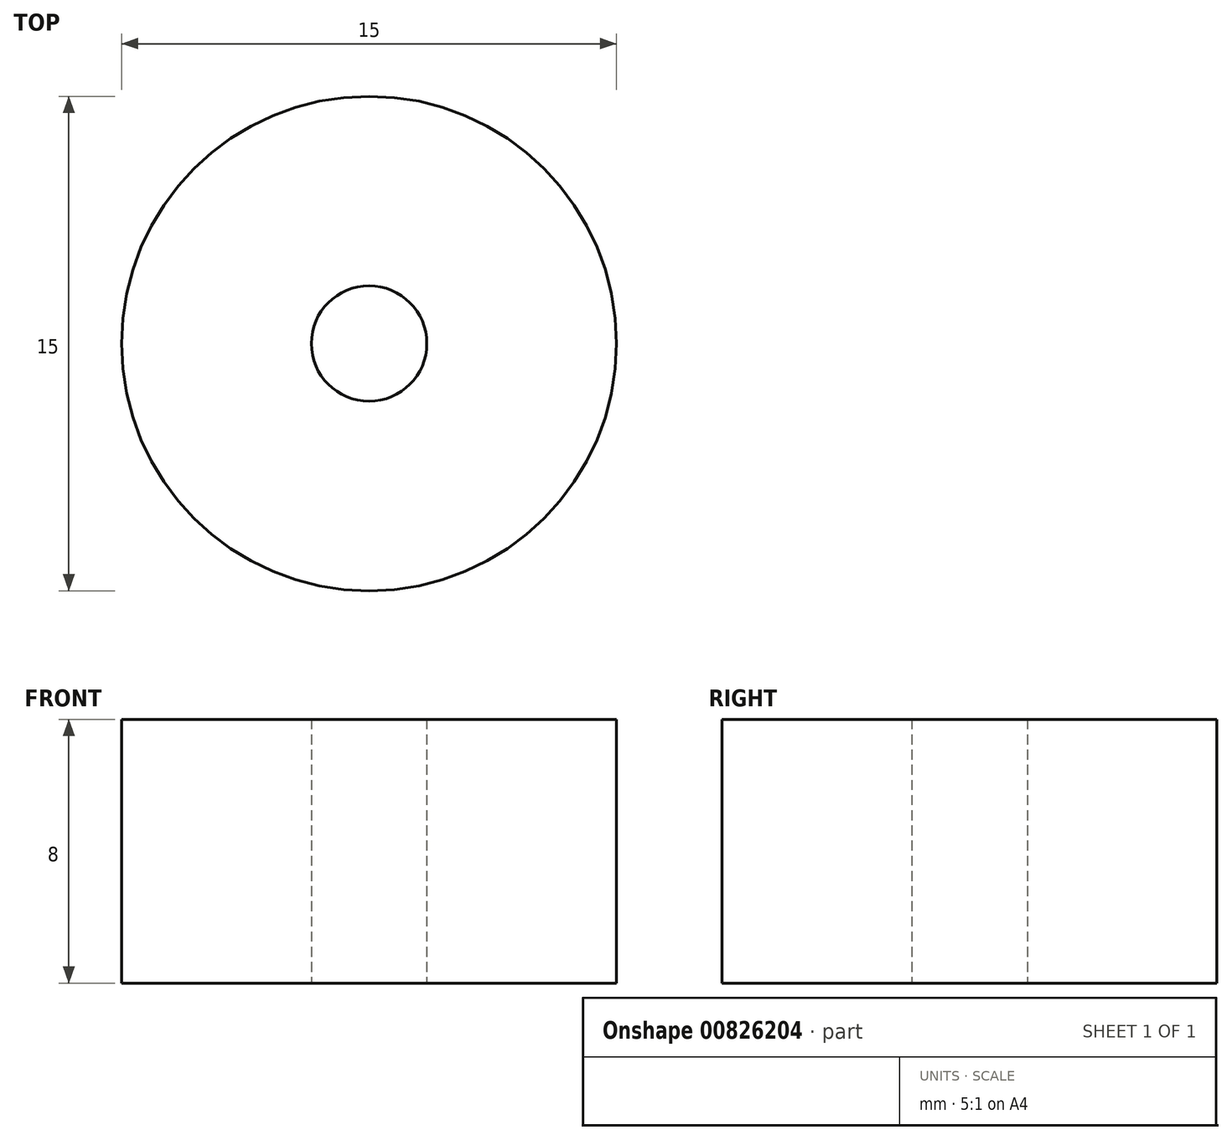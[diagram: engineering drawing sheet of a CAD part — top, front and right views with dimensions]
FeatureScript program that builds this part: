
annotation { "Feature Type Name" : "Feature", "Feature Type Description" : "" }
export const myFeature = defineFeature(function(context is Context, id is Id, definition is map)
    precondition{}
    {
        {
            var Q0;
            Q0=qCreatedBy(makeId("Top.planeOp"),FACE);
            var sketch = newSketch(context, id + "F0", { "sketchPlane" : qUnion([Q0])});
            skCircle(sketch, "E0", {"center": v(0, 0) * mm, "radius": 1.75 * mm});
            skCircle(sketch, "E1", {"center": v(0, 0) * mm, "radius": 7.5 * mm});
            skSolve(sketch);
        }
        {
            var Q0;
            Q0=makeQuery(id+"F0.imprint","IMPRINT",FACE,{"disambiguationData":[TD([[makeQuery(id+"F0.imprint","IMPRINT",EDGE,{"derivedFrom":sQuery(id+"F0.wireOp",EDGE,"E0")}),-1.0]])]});
            extrude(context, id + "F1", {"entities" : qUnion([Q0]), "depth" : 8 * mm, "offsetDistance" : 25 * mm});
        }
    });
